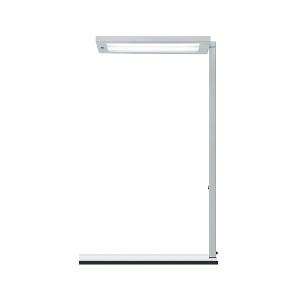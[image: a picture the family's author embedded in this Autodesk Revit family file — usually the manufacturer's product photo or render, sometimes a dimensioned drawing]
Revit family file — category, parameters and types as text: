
# Revit family: lavigo_core_-_dpt_12500_840_r_g1_ws_00812477_5b57
name_source: partatom
category: Lighting Fixtures
units: mm (PartAtom-declared; Revit-internal decimal feet)

## family parameters
Cut with Voids When Loaded = No
Host = Face
Light Source = No
Part Type = Normal
Room Calculation Point = No
Round Connector Dimension = Use Diameter
Shared = No

## types (1)
- LAVIGO.core - DPT 12500/840/R/G1/WS (1 x LED, 12400 lm, 4000K)
    Apparent Load = 85 VA
    Approval mark = CE
    CIE Flux Codes = 58 87 97 17 100
    Color Rendering = 80-89
    Color Temperature = 4000K
    Control Gear = Electronic ballast
    Default Elevation = 1800 mm
    Description = DPT 12500/840/R/G1|Desk-mounted luminaire|light source: LED Cold white   |work equipment: Electronic ballast DALI|connected load: 220-240 V, 50/60 Hz|Power consumption: approx. 85 W|standby: approx. 0,30|power factor: approx. 0,973|luminous flux: 12500 lm|luminous efficacy: 147 lm/W|light distribution: Direct/indirect|direct ratio: approx. 17 %|color rendering index (CRI): >= 80|chromaticity tolerance:  3 SDCM|technology: Presence and daylight sensor control (PIR)|operation: Rocker switch|luminaire body|material: Steel/plastic|surface: Painted|colour: White|lamp cover: Polycarbonate (PC), Clear|tubular section|material: Steel tube|surface: Painted|Form: Tubular section upright|colour of tubular section: White|weight (net): approx. 8.3 kg|mains lead: 3.70 m Mains plug CEE 7/VII|Fastening: Socket, Table adaptor|decorative contrast side parts: Flint grey|glare control: Prism aperture|luminance(L65): <= 3000 cd/m|unified glare rating(4H 8H): <=  16|special features: Luminaire head detachable, Direct and indirect light switchable together, Flicker-free, Integrated light and presence sensor PIR, Motion sensor time-out of 15mins~|
    Frequency = 50 Hz, 60 Hz
    Height = 36 mm
    Lamp = 1 x LED
    Lamp Light Flux = 12400 lm
    Lamp count = 1
    Length = 675 mm
    Luminous efficacy = 146 lm/W
    Manufacturer = Waldmann
    ModVariant = No
    Model = 00812477
    Mounting Place = Floor
    Mounting Type = Freestanding
    Number of Poles = 1
    OnlyDefault = Yes
    Power Factor = 1
    Product Name = LAVIGO.core - DPT 12500/840/R/G1/WS
    Product group = Desk mounted luminaire with detector
    ProductGroupID = 2201
    Protection Class = Protection class I
    Protection Degree = IP 20
    RLX_Detail_Level = 1
    RLX_Emergency_Light_Flux = 0 lm
    RLX_Emergency_Type = 0
    RLX_Emergency_Type_DB = No
    RlxData = <blob elided: 31093 chars, md5=f40ad2db>
    Socket = socket
    Standby Power = 0 W
    System Light Flux = 12400 lm
    System Power = 85 W
    Type Comments = Product without accessories
    Type Image = 121808000-00758540.jpg
    URL = http://relux.com
    VarID = ---
    Voltage = 230 V
    Voltage Range = 220-240 V
    Weight = 0.00 kg
    Width = 320 mm

## geometry (parser evidence)
native form markers: Blend x4, Sweep x17
no freeform markers — native parametric forms only
